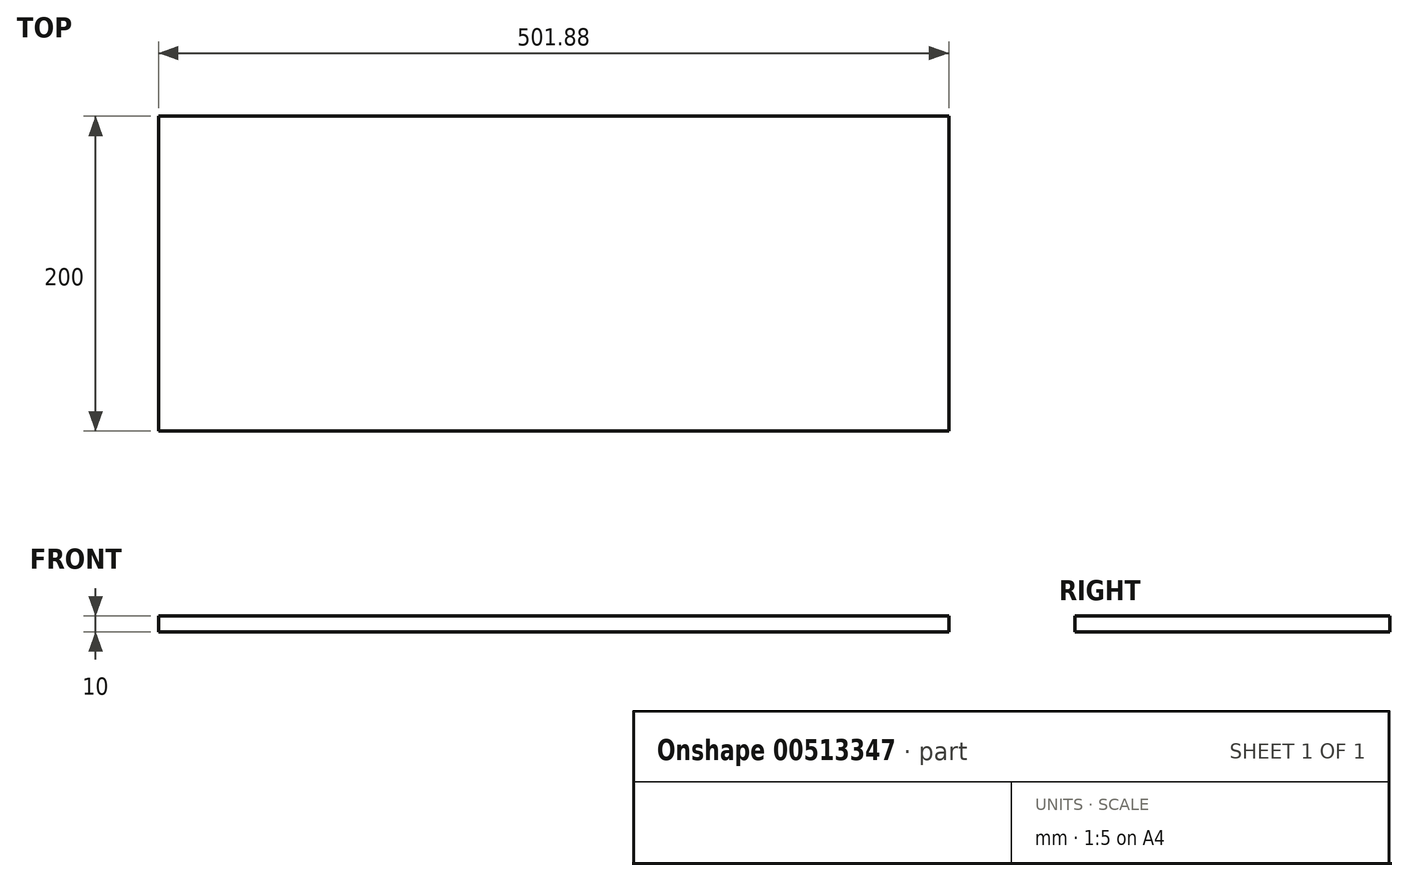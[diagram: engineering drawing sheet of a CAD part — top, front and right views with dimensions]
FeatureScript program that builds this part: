
annotation { "Feature Type Name" : "Feature", "Feature Type Description" : "" }
export const myFeature = defineFeature(function(context is Context, id is Id, definition is map)
    precondition{}
    {
        {
            var Q0;
            Q0=qCreatedBy(makeId("Front.planeOp"),FACE);
            var sketch = newSketch(context, id + "F0", { "sketchPlane" : qUnion([Q0])});
            skLineSegment(sketch, "E0.bottom", {"start": v(0, 0) * mm, "end": v(501.88, 0) * mm});
            skLineSegment(sketch, "E0.top", {"start": v(0, 10) * mm, "end": v(501.88, 10) * mm});
            skLineSegment(sketch, "E0.left", {"start": v(0, 0) * mm, "end": v(0, 10) * mm});
            skLineSegment(sketch, "E0.right", {"start": v(501.88, 0) * mm, "end": v(501.88, 10) * mm});
            skSolve(sketch);
        }
        {
            var Q0;
            Q0 = qSketchRegion(id + "F0", true);
            extrude(context, id + "F1", {"entities" : qUnion([Q0]), "depth" : 200 * mm});
        }
    });
